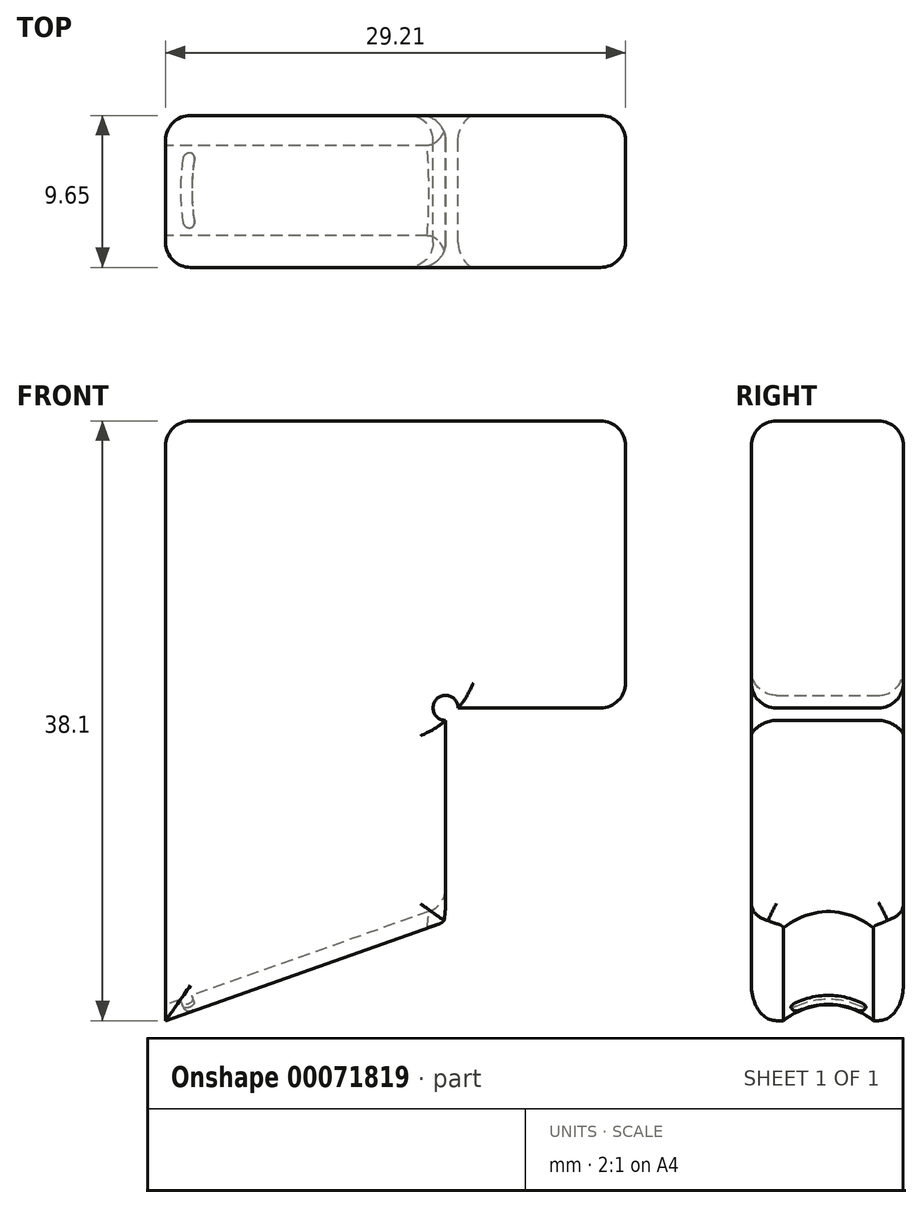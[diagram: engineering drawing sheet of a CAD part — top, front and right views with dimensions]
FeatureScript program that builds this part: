
annotation { "Feature Type Name" : "Feature", "Feature Type Description" : "" }
export const myFeature = defineFeature(function(context is Context, id is Id, definition is map)
    precondition{}
    {
        {
            var Q0;
            Q0=qCreatedBy(makeId("Front.planeOp"),FACE);
            var sketch = newSketch(context, id + "F0", { "sketchPlane" : qUnion([Q0])});
            skLineSegment(sketch, "E0", {"start": v(0, 0) * mm, "end": v(0, -38.1) * mm});
            skLineSegment(sketch, "E1", {"start": v(0, -38.1) * mm, "end": v(29.21, -27.76) * mm});
            skLineSegment(sketch, "E2", {"start": v(29.21, -27.76) * mm, "end": v(29.21, 0) * mm});
            skLineSegment(sketch, "E3", {"start": v(29.2, 0) * mm, "end": v(0, 0) * mm});
            skLineSegment(sketch, "E4", {"start": v(29.21, -18.23) * mm, "end": v(17.78, -18.23) * mm});
            skLineSegment(sketch, "E5", {"start": v(17.78, -18.23) * mm, "end": v(17.78, -31.8) * mm});
            skCircle(sketch, "E6", {"center": v(17.78, -18.23) * mm, "radius": 0.8 * mm});
            skSolve(sketch);
        }
        {
            var Q0;
            Q0=makeQuery(id+"F0.imprint","IMPRINT",FACE,{"disambiguationData":[TD([[makeQuery(id+"F0.imprint","IMPRINT",EDGE,{"derivedFrom":sQuery(id+"F0.wireOp",EDGE,"E0")}),1.0]])]});
            extrude(context, id + "F1", {"entities" : qUnion([Q0]), "depth" : 9.65 * mm, "offsetDistance" : 25.4 * mm});
        }
        {
            var Q0;
            Q0=makeQuery(id+"F1.opExtrude","SWEPT_FACE",FACE,{"disambiguationData":[OSD([sQuery(id+"F0.wireOp",EDGE,"E0")])]});
            var Q1;
            Q1=makeQuery(id+"F1.opExtrude","SWEPT_EDGE",EDGE,{"disambiguationData":[OSD([sQuery(id+"F0.wireOp",EDGE,"E0"),sQuery(id+"F0.wireOp",EDGE,"E1")])]});
            cPlane(context, id + "F2", {"entities" : qUnion([Q0, Q1]), "cplaneType" : CPlaneType.LINE_ANGLE, "offset" : 25.4 * mm, "angle" : 19.5 * degree, "oppositeDirection" : true, "width" : 152.4 * mm, "height" : 152.4 * mm});
        }
        {
            var Q0;
            Q0=qCreatedBy(id+"F2.planeOp",FACE);
            var sketch = newSketch(context, id + "F3", { "sketchPlane" : qUnion([Q0])});
            skCircle(sketch, "E7", {"center": v(-4.76, -39.72) * mm, "radius": 4.76 * mm});
            skSolve(sketch);
        }
        {
            var Q0;
            Q0=makeQuery(id+"F3.imprint","IMPRINT",FACE,{"disambiguationData":[TD([[makeQuery(id+"F3.imprint","IMPRINT",EDGE,{"derivedFrom":sQuery(id+"F3.wireOp",EDGE,"E7")}),1.0]])]});
            extrude(context, id + "F4", {"entities" : qUnion([Q0]), "operationType" : NewBodyOperationType.REMOVE, "depth" : 25.4 * mm, "offsetDistance" : 25.4 * mm});
        }
        {
            var Q0;
            Q0=makeQuery(id+"F1.opExtrude","CAP_FACE",FACE,{"disambiguationData":[OSD([sQuery(id+"F0.wireOp",EDGE,"E0"),sQuery(id+"F0.wireOp",EDGE,"E1"),sQuery(id+"F0.wireOp",EDGE,"E2"),sQuery(id+"F0.wireOp",EDGE,"E3"),sQuery(id+"F0.wireOp",EDGE,"E4"),sQuery(id+"F0.wireOp",EDGE,"E5"),sQuery(id+"F0.wireOp",EDGE,"E6")])],"isStart":false});
            var Q1;
            Q1=makeQuery(id+"F1.opExtrude","CAP_FACE",FACE,{"disambiguationData":[OSD([sQuery(id+"F0.wireOp",EDGE,"E0"),sQuery(id+"F0.wireOp",EDGE,"E1"),sQuery(id+"F0.wireOp",EDGE,"E2"),sQuery(id+"F0.wireOp",EDGE,"E3"),sQuery(id+"F0.wireOp",EDGE,"E4"),sQuery(id+"F0.wireOp",EDGE,"E5"),sQuery(id+"F0.wireOp",EDGE,"E6")])],"isStart":true});
            var Q2;
            Q2=makeQuery(id+"F1.opExtrude","SWEPT_EDGE",EDGE,{"disambiguationData":[OSD([sQuery(id+"F0.wireOp",EDGE,"E2"),sQuery(id+"F0.wireOp",EDGE,"E3")])]});
            var Q3;
            Q3=makeQuery(id+"F1.opExtrude","SWEPT_EDGE",EDGE,{"disambiguationData":[OSD([sQuery(id+"F0.wireOp",EDGE,"E0"),sQuery(id+"F0.wireOp",EDGE,"E3")])]});
            var Q4;
            Q4=makeQuery(id+"F1.opExtrude","SWEPT_EDGE",EDGE,{"disambiguationData":[OSD([sQuery(id+"F0.wireOp",EDGE,"E2"),sQuery(id+"F0.wireOp",EDGE,"E4")])]});
            fillet(context, id + "F5", {"entities" : qUnion([Q0, Q1, Q2, Q3, Q4]), "radius" : 1.59 * mm, "tangentPropagation" : true, "allowEdgeOverflow" : false});
        }
        {
            var Q0;
            Q0=makeQuery(id+"F4.boolean.opBoolean","INTERSECT",EDGE,{"derivedFrom":[makeQuery(id+"F1.opExtrude","SWEPT_FACE",FACE,{"disambiguationData":[OSD([sQuery(id+"F0.wireOp",EDGE,"E5")])]}),makeQuery(id+"F4.opExtrude","SWEPT_FACE",FACE,{"disambiguationData":[OSD([sQuery(id+"F3.wireOp",EDGE,"E7")])]})]});
            fillet(context, id + "F6", {"entities" : qUnion([Q0]), "radius" : 1.59 * mm, "tangentPropagation" : true, "allowEdgeOverflow" : false});
        }
        {
            var Q0;
            Q0=qCreatedBy(id+"F2.planeOp",FACE);
            cPlane(context, id + "F7", {"entities" : qUnion([Q0]), "cplaneType" : CPlaneType.OFFSET, "offset" : 1.73 * mm, "width" : 152.4 * mm, "height" : 152.4 * mm});
        }
        {
            var Q0;
            Q0=qCreatedBy(id+"F7.planeOp",FACE);
            var sketch = newSketch(context, id + "F8", { "sketchPlane" : qUnion([Q0])});
            skCircle(sketch, "E8", {"center": v(-4.76, -39.72) * mm, "radius": 4.32 * mm});
            skCircle(sketch, "E9", {"center": v(-4.76, -39.72) * mm, "radius": 4.76 * mm});
            skLineSegment(sketch, "E10", {"start": v(-4.76, -39.72) * mm, "end": v(-2.38, -35.6) * mm});
            skLineSegment(sketch, "E11", {"start": v(-4.76, -39.72) * mm, "end": v(-4.76, -35.4) * mm, "construction": true});
            skLineSegment(sketch, "E12.MirrorCS", {"start": v(-4.76, -39.72) * mm, "end": v(-7.14, -35.6) * mm});
            skSolve(sketch);
        }
        {
            var Q0;
            {var subQ0=sQuery(id+"F8.wireOp",EDGE,"E10");var subQ1=sQuery(id+"F8.wireOp",EDGE,"E8");var subQ2=makeQuery(id+"F8.imprint","INTERSECT",VERTEX,{"derivedFrom":[subQ1,subQ0]});Q0=makeQuery(id+"F8.imprint","IMPRINT",FACE,{"disambiguationData":[TD([[makeQuery(id+"F8.imprint","IMPRINT",EDGE,{"disambiguationData":[TD([[subQ2,-1.0]])],"derivedFrom":subQ1}),-1.0]])]});}
            extrude(context, id + "F9", {"entities" : qUnion([Q0]), "operationType" : NewBodyOperationType.ADD, "depth" : 0.76 * mm, "offsetDistance" : 25.4 * mm, "symmetric" : true});
        }
        {
            var Q0;
            Q0=makeQuery(id+"F9.opExtrude","CAP_EDGE",EDGE,{"disambiguationData":[OSD([sQuery(id+"F8.wireOp",EDGE,"E8")])],"isStart":true});
            var Q1;
            Q1=makeQuery(id+"F9.opExtrude","CAP_EDGE",EDGE,{"disambiguationData":[OSD([sQuery(id+"F8.wireOp",EDGE,"E8")])],"isStart":false});
            fillet(context, id + "F10", {"entities" : qUnion([Q0, Q1]), "radius" : 0.38 * mm, "tangentPropagation" : true, "allowEdgeOverflow" : false});
        }
        {
            var Q0;
            Q0=makeQuery(id+"F10.opFillet","BLEND_EDGE",EDGE,{"blendedFrom":[makeQuery(id+"F9.opExtrude","CAP_EDGE",EDGE,{"disambiguationData":[OSD([sQuery(id+"F8.wireOp",EDGE,"E8")])],"isStart":true}),makeQuery(id+"F9.opExtrude","SWEPT_FACE",FACE,{"disambiguationData":[OSD([sQuery(id+"F8.wireOp",EDGE,"E10")])]})],"blendedInto":[makeQuery(id+"F9.opExtrude","SWEPT_FACE",FACE,{"disambiguationData":[OSD([sQuery(id+"F8.wireOp",EDGE,"E10")])]})]});
            var Q1;
            Q1=makeQuery(id+"F10.opFillet","BLEND_EDGE",EDGE,{"blendedFrom":[makeQuery(id+"F9.opExtrude","CAP_EDGE",EDGE,{"disambiguationData":[OSD([sQuery(id+"F8.wireOp",EDGE,"E8")])],"isStart":true}),makeQuery(id+"F9.opExtrude","SWEPT_FACE",FACE,{"disambiguationData":[OSD([sQuery(id+"F8.wireOp",EDGE,"E12.MirrorCS")])]})],"blendedInto":[makeQuery(id+"F9.opExtrude","SWEPT_FACE",FACE,{"disambiguationData":[OSD([sQuery(id+"F8.wireOp",EDGE,"E12.MirrorCS")])]})]});
            fillet(context, id + "F11", {"entities" : qUnion([Q0, Q1]), "radius" : 0.38 * mm, "tangentPropagation" : true, "allowEdgeOverflow" : false});
        }
    });
